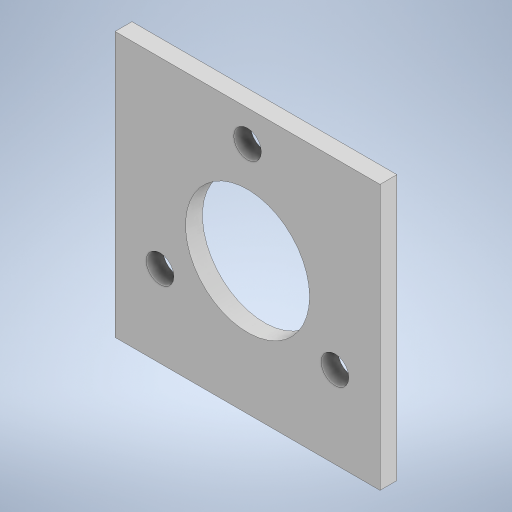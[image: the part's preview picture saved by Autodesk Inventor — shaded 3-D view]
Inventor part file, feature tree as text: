
AUTODESK INVENTOR PART (.ipt)
format: ipt  version: 2024 (Build 280153000, 153)  size: 236,032 bytes
history: native  units: in
note: dims shown in document units (in); Inventor stores cm internally (conversion verified against a paired STEP export)
features: extrude x1, sketch x1
ambient origin geometry x8: Origin, YZ Plane, XZ Plane, XY Plane, X Axis, Y Axis, Z Axis, Center Point
bodies: Body1 (feature_tree)
feature tree (2):
  extrude  "Extrusion2"  Depth=1.8504in
  sketch  "Sketch1"  dims[d0=1.8504in d1=1.8504in d2=0.8661in d3=0.7069in d4=0.6108in d5=120.0deg d6=0.6108in d7=120.0deg d8=0.1929in d9=0.1929in d10=0.1929in d16=0.1181in d17=0.0in d11=0.0197in d12=0.0344in d13=0.0197in d14=0.0344in]
